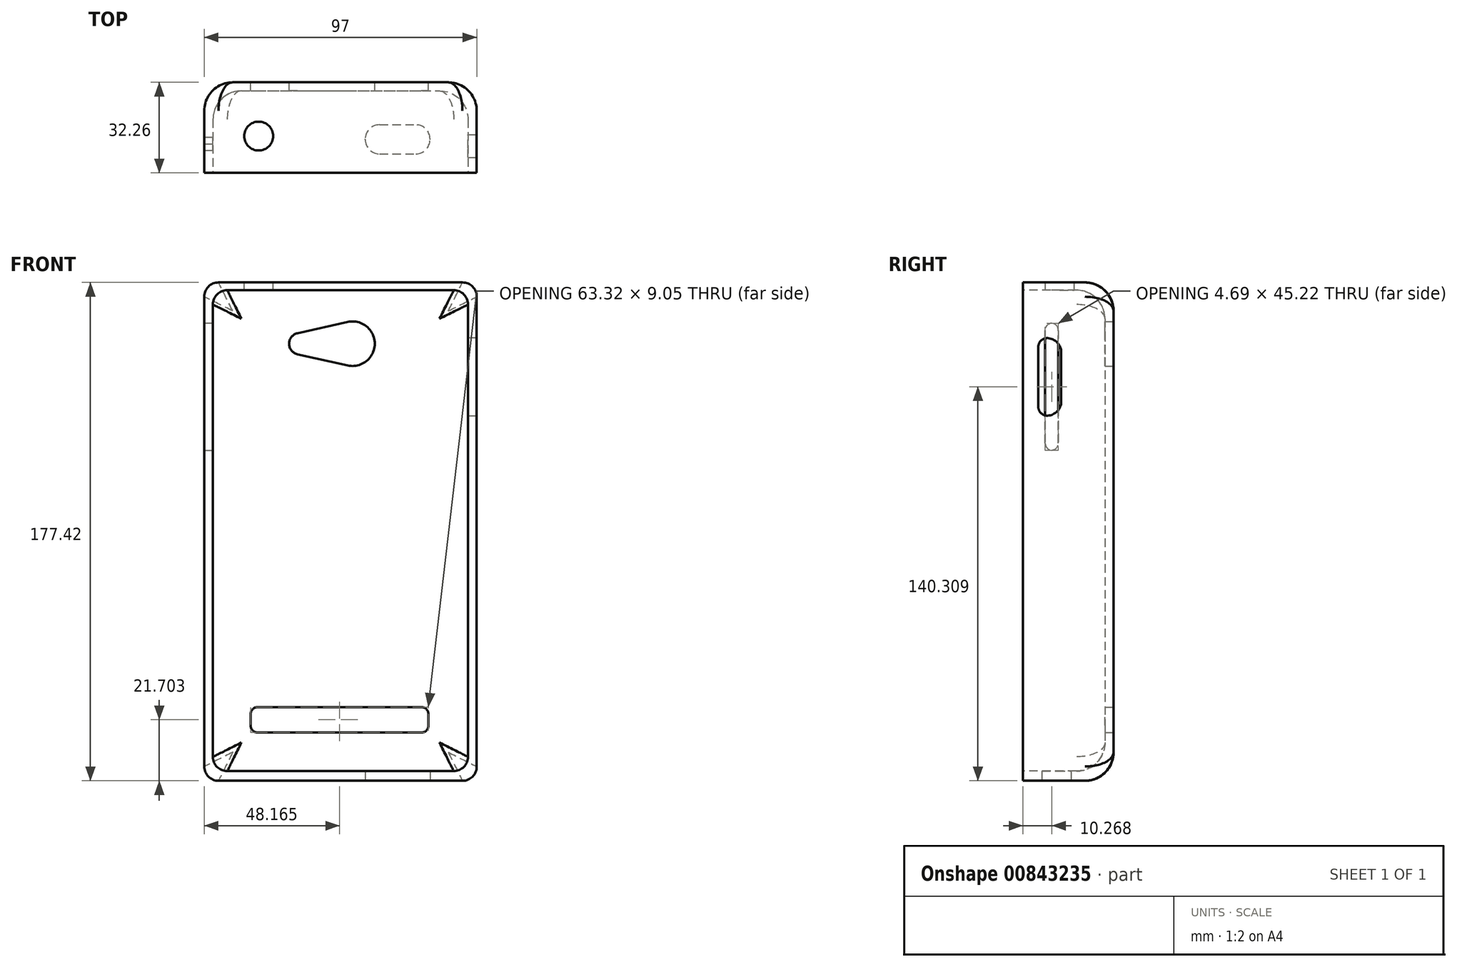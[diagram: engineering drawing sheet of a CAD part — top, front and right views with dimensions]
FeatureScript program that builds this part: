
annotation { "Feature Type Name" : "Feature", "Feature Type Description" : "" }
export const myFeature = defineFeature(function(context is Context, id is Id, definition is map)
    precondition{}
    {
        {
            var Q0;
            Q0=qCreatedBy(makeId("Front.planeOp"),FACE);
            var sketch = newSketch(context, id + "F0", { "sketchPlane" : qUnion([Q0])});
            skLineSegment(sketch, "E0.bottom", {"start": v(-48.5, 102.73) * mm, "end": v(48.5, 102.73) * mm});
            skLineSegment(sketch, "E0.top", {"start": v(-48.5, -74.69) * mm, "end": v(48.5, -74.69) * mm});
            skLineSegment(sketch, "E0.left", {"start": v(-48.5, 102.73) * mm, "end": v(-48.5, -74.69) * mm});
            skLineSegment(sketch, "E0.right", {"start": v(48.5, 102.73) * mm, "end": v(48.5, -74.69) * mm});
            skSolve(sketch);
        }
        {
            var Q0;
            Q0=makeQuery(id+"F0.imprint","IMPRINT",FACE,{"disambiguationData":[TD([[makeQuery(id+"F0.imprint","IMPRINT",EDGE,{"derivedFrom":sQuery(id+"F0.wireOp",EDGE,"E0.bottom")}),-1.0]])]});
            extrude(context, id + "F1", {"entities" : qUnion([Q0]), "depth" : 32.26 * mm, "offsetDistance" : 25.4 * mm});
        }
        {
            var Q0;
            Q0=makeQuery(id+"F1.opExtrude","CAP_FACE",FACE,{"disambiguationData":[OSD([sQuery(id+"F0.wireOp",EDGE,"E0.bottom"),sQuery(id+"F0.wireOp",EDGE,"E0.top"),sQuery(id+"F0.wireOp",EDGE,"E0.left"),sQuery(id+"F0.wireOp",EDGE,"E0.right")])],"isStart":false});
            var sketch = newSketch(context, id + "F2", { "sketchPlane" : qUnion([Q0])});
            skLineSegment(sketch, "E1.bottom", {"start": v(-45.4, 99.96) * mm, "end": v(45.4, 99.96) * mm});
            skLineSegment(sketch, "E1.top", {"start": v(-45.4, -71.25) * mm, "end": v(45.4, -71.25) * mm});
            skLineSegment(sketch, "E1.left", {"start": v(-45.4, 99.96) * mm, "end": v(-45.4, -71.25) * mm});
            skLineSegment(sketch, "E1.right", {"start": v(45.4, 99.96) * mm, "end": v(45.4, -71.25) * mm});
            skSolve(sketch);
        }
        {
            var Q0;
            Q0=makeQuery(id+"F2.imprint","IMPRINT",FACE,{"disambiguationData":[TD([[makeQuery(id+"F2.imprint","IMPRINT",EDGE,{"derivedFrom":sQuery(id+"F2.wireOp",EDGE,"E1.bottom")}),-1.0]])]});
            extrude(context, id + "F3", {"entities" : qUnion([Q0]), "operationType" : NewBodyOperationType.REMOVE, "oppositeDirection" : true, "depth" : 29.2 * mm, "offsetDistance" : 25.4 * mm});
        }
        {
            var Q0;
            Q0=makeQuery(id+"F1.opExtrude","CAP_FACE",FACE,{"disambiguationData":[OSD([sQuery(id+"F0.wireOp",EDGE,"E0.bottom"),sQuery(id+"F0.wireOp",EDGE,"E0.top"),sQuery(id+"F0.wireOp",EDGE,"E0.left"),sQuery(id+"F0.wireOp",EDGE,"E0.right")])],"isStart":true});
            var sketch = newSketch(context, id + "F4", { "sketchPlane" : qUnion([Q0])});
            skArc(sketch, "E2", {"start": v(-2.52, 88.67) * mm, "mid": v(-12.2, 80.92) * mm, "end": v(-2.52, 73.17) * mm});
            skArc(sketch, "E3", {"start": v(15.29, 77.17) * mm, "mid": v(18.29, 80.92) * mm, "end": v(15.29, 84.67) * mm});
            skLineSegment(sketch, "E4", {"start": v(-2.52, 88.67) * mm, "end": v(15.29, 84.67) * mm});
            skLineSegment(sketch, "E5", {"start": v(15.29, 77.17) * mm, "end": v(-2.52, 73.17) * mm});
            skSolve(sketch);
        }
        {
            var Q0;
            Q0=makeQuery(id+"F4.imprint","IMPRINT",FACE,{"disambiguationData":[TD([[makeQuery(id+"F4.imprint","IMPRINT",EDGE,{"derivedFrom":sQuery(id+"F4.wireOp",EDGE,"E2")}),1.0]])]});
            extrude(context, id + "F5", {"entities" : qUnion([Q0]), "operationType" : NewBodyOperationType.REMOVE, "oppositeDirection" : true, "depth" : 76.7 * mm, "offsetDistance" : 25.4 * mm});
        }
        {
            var Q0;
            Q0=makeQuery(id+"F1.opExtrude","SWEPT_EDGE",EDGE,{"disambiguationData":[OSD([sQuery(id+"F0.wireOp",EDGE,"E0.bottom"),sQuery(id+"F0.wireOp",EDGE,"E0.right")])]});
            var Q1;
            Q1=makeQuery(id+"F3.boolean.opBoolean","COPY",EDGE,{"derivedFrom":makeQuery(id+"F3.opExtrude","SWEPT_EDGE",EDGE,{"disambiguationData":[OSD([sQuery(id+"F2.wireOp",EDGE,"E1.bottom"),sQuery(id+"F2.wireOp",EDGE,"E1.right")])]})});
            var Q2;
            Q2=makeQuery(id+"F1.opExtrude","SWEPT_EDGE",EDGE,{"disambiguationData":[OSD([sQuery(id+"F0.wireOp",EDGE,"E0.bottom"),sQuery(id+"F0.wireOp",EDGE,"E0.left")])]});
            var Q3;
            Q3=makeQuery(id+"F3.boolean.opBoolean","COPY",EDGE,{"derivedFrom":makeQuery(id+"F3.opExtrude","SWEPT_EDGE",EDGE,{"disambiguationData":[OSD([sQuery(id+"F2.wireOp",EDGE,"E1.bottom"),sQuery(id+"F2.wireOp",EDGE,"E1.left")])]})});
            var Q4;
            Q4=makeQuery(id+"F1.opExtrude","SWEPT_EDGE",EDGE,{"disambiguationData":[OSD([sQuery(id+"F0.wireOp",EDGE,"E0.top"),sQuery(id+"F0.wireOp",EDGE,"E0.right")])]});
            var Q5;
            Q5=makeQuery(id+"F3.boolean.opBoolean","COPY",EDGE,{"derivedFrom":makeQuery(id+"F3.opExtrude","SWEPT_EDGE",EDGE,{"disambiguationData":[OSD([sQuery(id+"F2.wireOp",EDGE,"E1.top"),sQuery(id+"F2.wireOp",EDGE,"E1.right")])]})});
            var Q6;
            Q6=makeQuery(id+"F1.opExtrude","SWEPT_EDGE",EDGE,{"disambiguationData":[OSD([sQuery(id+"F0.wireOp",EDGE,"E0.top"),sQuery(id+"F0.wireOp",EDGE,"E0.left")])]});
            var Q7;
            Q7=makeQuery(id+"F3.boolean.opBoolean","COPY",EDGE,{"derivedFrom":makeQuery(id+"F3.opExtrude","SWEPT_EDGE",EDGE,{"disambiguationData":[OSD([sQuery(id+"F2.wireOp",EDGE,"E1.top"),sQuery(id+"F2.wireOp",EDGE,"E1.left")])]})});
            fillet(context, id + "F6", {"entities" : qUnion([Q0, Q1, Q2, Q3, Q4, Q5, Q6, Q7]), "radius" : 5.08 * mm, "tangentPropagation" : true, "allowEdgeOverflow" : false});
        }
        {
            var Q0;
            Q0=makeQuery(id+"F1.opExtrude","CAP_EDGE",EDGE,{"disambiguationData":[OSD([sQuery(id+"F0.wireOp",EDGE,"E0.right")])],"isStart":true});
            var Q1;
            Q1=makeQuery(id+"F3.boolean.opBoolean","COPY",EDGE,{"derivedFrom":makeQuery(id+"F3.opExtrude","CAP_EDGE",EDGE,{"disambiguationData":[OSD([sQuery(id+"F2.wireOp",EDGE,"E1.left")])],"isStart":false})});
            fillet(context, id + "F7", {"entities" : qUnion([Q0, Q1]), "radius" : 10.16 * mm, "tangentPropagation" : true, "allowEdgeOverflow" : false});
        }
        {
            var Q0;
            Q0=makeQuery(id+"F1.opExtrude","SWEPT_FACE",FACE,{"disambiguationData":[OSD([sQuery(id+"F0.wireOp",EDGE,"E0.top")])]});
            var sketch = newSketch(context, id + "F8", { "sketchPlane" : qUnion([Q0])});
            skLineSegment(sketch, "E6.bottom", {"start": v(8.82, 25.47) * mm, "end": v(31.87, 25.47) * mm});
            skLineSegment(sketch, "E6.top", {"start": v(8.82, 15.13) * mm, "end": v(31.87, 15.13) * mm});
            skLineSegment(sketch, "E6.left", {"start": v(8.82, 25.47) * mm, "end": v(8.82, 15.13) * mm});
            skLineSegment(sketch, "E6.right", {"start": v(31.87, 25.47) * mm, "end": v(31.87, 15.13) * mm});
            skSolve(sketch);
        }
        {
            var Q0;
            Q0=makeQuery(id+"F8.imprint","IMPRINT",FACE,{"disambiguationData":[TD([[makeQuery(id+"F8.imprint","IMPRINT",EDGE,{"derivedFrom":sQuery(id+"F8.wireOp",EDGE,"E6.bottom")}),-1.0]])]});
            extrude(context, id + "F9", {"entities" : qUnion([Q0]), "operationType" : NewBodyOperationType.REMOVE, "oppositeDirection" : true, "depth" : 18.29 * mm, "offsetDistance" : 25.4 * mm});
        }
        {
            var Q0;
            Q0=makeQuery(id+"F1.opExtrude","SWEPT_FACE",FACE,{"disambiguationData":[OSD([sQuery(id+"F0.wireOp",EDGE,"E0.bottom")])]});
            var sketch = newSketch(context, id + "F10", { "sketchPlane" : qUnion([Q0])});
            skCircle(sketch, "E7", {"center": v(-29.13, -19.14) * mm, "radius": 5.14 * mm});
            skSolve(sketch);
        }
        {
            var Q0;
            Q0=makeQuery(id+"F10.imprint","IMPRINT",FACE,{"disambiguationData":[TD([[makeQuery(id+"F10.imprint","IMPRINT",EDGE,{"derivedFrom":sQuery(id+"F10.wireOp",EDGE,"E7")}),1.0]])]});
            extrude(context, id + "F11", {"entities" : qUnion([Q0]), "operationType" : NewBodyOperationType.REMOVE, "oppositeDirection" : true, "depth" : 27.94 * mm, "offsetDistance" : 25.4 * mm});
        }
        {
            var Q0;
            Q0=makeQuery(id+"F1.opExtrude","CAP_FACE",FACE,{"disambiguationData":[OSD([sQuery(id+"F0.wireOp",EDGE,"E0.bottom"),sQuery(id+"F0.wireOp",EDGE,"E0.top"),sQuery(id+"F0.wireOp",EDGE,"E0.left"),sQuery(id+"F0.wireOp",EDGE,"E0.right")])],"isStart":true});
            var sketch = newSketch(context, id + "F12", { "sketchPlane" : qUnion([Q0])});
            skLineSegment(sketch, "E8.bottom", {"start": v(-31.33, -48.46) * mm, "end": v(32, -48.46) * mm});
            skLineSegment(sketch, "E8.top", {"start": v(-31.33, -57.51) * mm, "end": v(32, -57.51) * mm});
            skLineSegment(sketch, "E8.left", {"start": v(-31.33, -48.46) * mm, "end": v(-31.33, -57.51) * mm});
            skLineSegment(sketch, "E8.right", {"start": v(32, -48.46) * mm, "end": v(32, -57.51) * mm});
            skSolve(sketch);
        }
        {
            var Q0;
            Q0=makeQuery(id+"F12.imprint","IMPRINT",FACE,{"disambiguationData":[TD([[makeQuery(id+"F12.imprint","IMPRINT",EDGE,{"derivedFrom":sQuery(id+"F12.wireOp",EDGE,"E8.bottom")}),-1.0]])]});
            extrude(context, id + "F13", {"entities" : qUnion([Q0]), "operationType" : NewBodyOperationType.REMOVE, "oppositeDirection" : true, "depth" : 25.4 * mm, "offsetDistance" : 25.4 * mm});
        }
        {
            var Q0;
            Q0=makeQuery(id+"F1.opExtrude","SWEPT_FACE",FACE,{"disambiguationData":[OSD([sQuery(id+"F0.wireOp",EDGE,"E0.left")])]});
            var sketch = newSketch(context, id + "F14", { "sketchPlane" : qUnion([Q0])});
            skLineSegment(sketch, "E9.bottom", {"start": v(19.65, 88.23) * mm, "end": v(24.34, 88.23) * mm});
            skLineSegment(sketch, "E9.top", {"start": v(19.65, 43) * mm, "end": v(24.34, 43) * mm});
            skLineSegment(sketch, "E9.left", {"start": v(19.65, 88.23) * mm, "end": v(19.65, 43) * mm});
            skLineSegment(sketch, "E9.right", {"start": v(24.34, 88.23) * mm, "end": v(24.34, 43) * mm});
            skSolve(sketch);
        }
        {
            var Q0;
            Q0=makeQuery(id+"F14.imprint","IMPRINT",FACE,{"disambiguationData":[TD([[makeQuery(id+"F14.imprint","IMPRINT",EDGE,{"derivedFrom":sQuery(id+"F14.wireOp",EDGE,"E9.bottom")}),-1.0]])]});
            extrude(context, id + "F15", {"entities" : qUnion([Q0]), "operationType" : NewBodyOperationType.REMOVE, "endBound" : BoundingType.UP_TO_NEXT, "oppositeDirection" : true, "depth" : 25.4 * mm, "offsetDistance" : 25.4 * mm});
        }
        {
            var Q0;
            Q0=makeQuery(id+"F15.boolean.opBoolean","COPY",EDGE,{"derivedFrom":makeQuery(id+"F15.opExtrude","SWEPT_EDGE",EDGE,{"disambiguationData":[OSD([sQuery(id+"F14.wireOp",EDGE,"E9.bottom"),sQuery(id+"F14.wireOp",EDGE,"E9.left")])]})});
            var Q1;
            Q1=makeQuery(id+"F15.boolean.opBoolean","COPY",EDGE,{"derivedFrom":makeQuery(id+"F15.opExtrude","SWEPT_EDGE",EDGE,{"disambiguationData":[OSD([sQuery(id+"F14.wireOp",EDGE,"E9.bottom"),sQuery(id+"F14.wireOp",EDGE,"E9.right")])]})});
            var Q2;
            Q2=makeQuery(id+"F15.boolean.opBoolean","COPY",EDGE,{"derivedFrom":makeQuery(id+"F15.opExtrude","SWEPT_EDGE",EDGE,{"disambiguationData":[OSD([sQuery(id+"F14.wireOp",EDGE,"E9.top"),sQuery(id+"F14.wireOp",EDGE,"E9.left")])]})});
            var Q3;
            Q3=makeQuery(id+"F15.boolean.opBoolean","COPY",EDGE,{"derivedFrom":makeQuery(id+"F15.opExtrude","SWEPT_EDGE",EDGE,{"disambiguationData":[OSD([sQuery(id+"F14.wireOp",EDGE,"E9.top"),sQuery(id+"F14.wireOp",EDGE,"E9.right")])]})});
            fillet(context, id + "F16", {"entities" : qUnion([Q0, Q1, Q2, Q3]), "radius" : 2.54 * mm, "tangentPropagation" : true, "allowEdgeOverflow" : false});
        }
        {
            var Q0;
            Q0=makeQuery(id+"F1.opExtrude","SWEPT_FACE",FACE,{"disambiguationData":[OSD([sQuery(id+"F0.wireOp",EDGE,"E0.right")])]});
            var sketch = newSketch(context, id + "F17", { "sketchPlane" : qUnion([Q0])});
            skLineSegment(sketch, "E10.bottom", {"start": v(-26.79, 82.91) * mm, "end": v(-18.62, 82.91) * mm});
            skLineSegment(sketch, "E10.top", {"start": v(-26.79, 55.3) * mm, "end": v(-18.62, 55.3) * mm});
            skLineSegment(sketch, "E10.left", {"start": v(-26.79, 82.91) * mm, "end": v(-26.79, 55.3) * mm});
            skLineSegment(sketch, "E10.right", {"start": v(-18.62, 82.91) * mm, "end": v(-18.62, 55.3) * mm});
            skSolve(sketch);
        }
        {
            var Q0;
            Q0=makeQuery(id+"F17.imprint","IMPRINT",FACE,{"disambiguationData":[TD([[makeQuery(id+"F17.imprint","IMPRINT",EDGE,{"derivedFrom":sQuery(id+"F17.wireOp",EDGE,"E10.bottom")}),-1.0]])]});
            extrude(context, id + "F18", {"entities" : qUnion([Q0]), "operationType" : NewBodyOperationType.REMOVE, "endBound" : BoundingType.UP_TO_NEXT, "oppositeDirection" : true, "depth" : 25.4 * mm, "offsetDistance" : 25.4 * mm});
        }
        {
            var Q0;
            Q0=makeQuery(id+"F18.boolean.opBoolean","COPY",EDGE,{"derivedFrom":makeQuery(id+"F18.opExtrude","SWEPT_EDGE",EDGE,{"disambiguationData":[OSD([sQuery(id+"F17.wireOp",EDGE,"E10.bottom"),sQuery(id+"F17.wireOp",EDGE,"E10.right")])]})});
            var Q1;
            Q1=makeQuery(id+"F18.boolean.opBoolean","COPY",EDGE,{"derivedFrom":makeQuery(id+"F18.opExtrude","SWEPT_EDGE",EDGE,{"disambiguationData":[OSD([sQuery(id+"F17.wireOp",EDGE,"E10.top"),sQuery(id+"F17.wireOp",EDGE,"E10.right")])]})});
            fillet(context, id + "F19", {"entities" : qUnion([Q0, Q1]), "radius" : 5.08 * mm, "tangentPropagation" : true, "allowEdgeOverflow" : false});
        }
        {
            var Q0;
            Q0=makeQuery(id+"F18.boolean.opBoolean","COPY",EDGE,{"derivedFrom":makeQuery(id+"F18.opExtrude","SWEPT_EDGE",EDGE,{"disambiguationData":[OSD([sQuery(id+"F17.wireOp",EDGE,"E10.top"),sQuery(id+"F17.wireOp",EDGE,"E10.left")])]})});
            var Q1;
            Q1=makeQuery(id+"F18.boolean.opBoolean","COPY",EDGE,{"derivedFrom":makeQuery(id+"F18.opExtrude","SWEPT_EDGE",EDGE,{"disambiguationData":[OSD([sQuery(id+"F17.wireOp",EDGE,"E10.bottom"),sQuery(id+"F17.wireOp",EDGE,"E10.left")])]})});
            fillet(context, id + "F20", {"entities" : qUnion([Q0, Q1]), "radius" : 3.17 * mm, "tangentPropagation" : true, "allowEdgeOverflow" : false});
        }
        {
            var Q0;
            Q0=makeQuery(id+"F9.boolean.opBoolean","COPY",EDGE,{"derivedFrom":makeQuery(id+"F9.opExtrude","SWEPT_EDGE",EDGE,{"disambiguationData":[OSD([sQuery(id+"F8.wireOp",EDGE,"E6.top"),sQuery(id+"F8.wireOp",EDGE,"E6.left")])]})});
            var Q1;
            Q1=makeQuery(id+"F9.boolean.opBoolean","COPY",EDGE,{"derivedFrom":makeQuery(id+"F9.opExtrude","SWEPT_EDGE",EDGE,{"disambiguationData":[OSD([sQuery(id+"F8.wireOp",EDGE,"E6.bottom"),sQuery(id+"F8.wireOp",EDGE,"E6.left")])]})});
            var Q2;
            Q2=makeQuery(id+"F9.boolean.opBoolean","COPY",EDGE,{"derivedFrom":makeQuery(id+"F9.opExtrude","SWEPT_EDGE",EDGE,{"disambiguationData":[OSD([sQuery(id+"F8.wireOp",EDGE,"E6.bottom"),sQuery(id+"F8.wireOp",EDGE,"E6.right")])]})});
            var Q3;
            Q3=makeQuery(id+"F9.boolean.opBoolean","COPY",EDGE,{"derivedFrom":makeQuery(id+"F9.opExtrude","SWEPT_EDGE",EDGE,{"disambiguationData":[OSD([sQuery(id+"F8.wireOp",EDGE,"E6.top"),sQuery(id+"F8.wireOp",EDGE,"E6.right")])]})});
            fillet(context, id + "F21", {"entities" : qUnion([Q0, Q1, Q2, Q3]), "radius" : 5.08 * mm, "tangentPropagation" : true, "allowEdgeOverflow" : false});
        }
        {
            var Q0;
            Q0=makeQuery(id+"F13.boolean.opBoolean","COPY",EDGE,{"derivedFrom":makeQuery(id+"F13.opExtrude","SWEPT_EDGE",EDGE,{"disambiguationData":[OSD([sQuery(id+"F12.wireOp",EDGE,"E8.top"),sQuery(id+"F12.wireOp",EDGE,"E8.left")])]})});
            var Q1;
            Q1=makeQuery(id+"F13.boolean.opBoolean","COPY",EDGE,{"derivedFrom":makeQuery(id+"F13.opExtrude","SWEPT_EDGE",EDGE,{"disambiguationData":[OSD([sQuery(id+"F12.wireOp",EDGE,"E8.bottom"),sQuery(id+"F12.wireOp",EDGE,"E8.left")])]})});
            var Q2;
            Q2=makeQuery(id+"F13.boolean.opBoolean","COPY",EDGE,{"derivedFrom":makeQuery(id+"F13.opExtrude","SWEPT_EDGE",EDGE,{"disambiguationData":[OSD([sQuery(id+"F12.wireOp",EDGE,"E8.bottom"),sQuery(id+"F12.wireOp",EDGE,"E8.right")])]})});
            var Q3;
            Q3=makeQuery(id+"F13.boolean.opBoolean","COPY",EDGE,{"derivedFrom":makeQuery(id+"F13.opExtrude","SWEPT_EDGE",EDGE,{"disambiguationData":[OSD([sQuery(id+"F12.wireOp",EDGE,"E8.top"),sQuery(id+"F12.wireOp",EDGE,"E8.right")])]})});
            fillet(context, id + "F22", {"entities" : qUnion([Q0, Q1, Q2, Q3]), "radius" : 2.54 * mm, "tangentPropagation" : true, "allowEdgeOverflow" : false});
        }
    });
